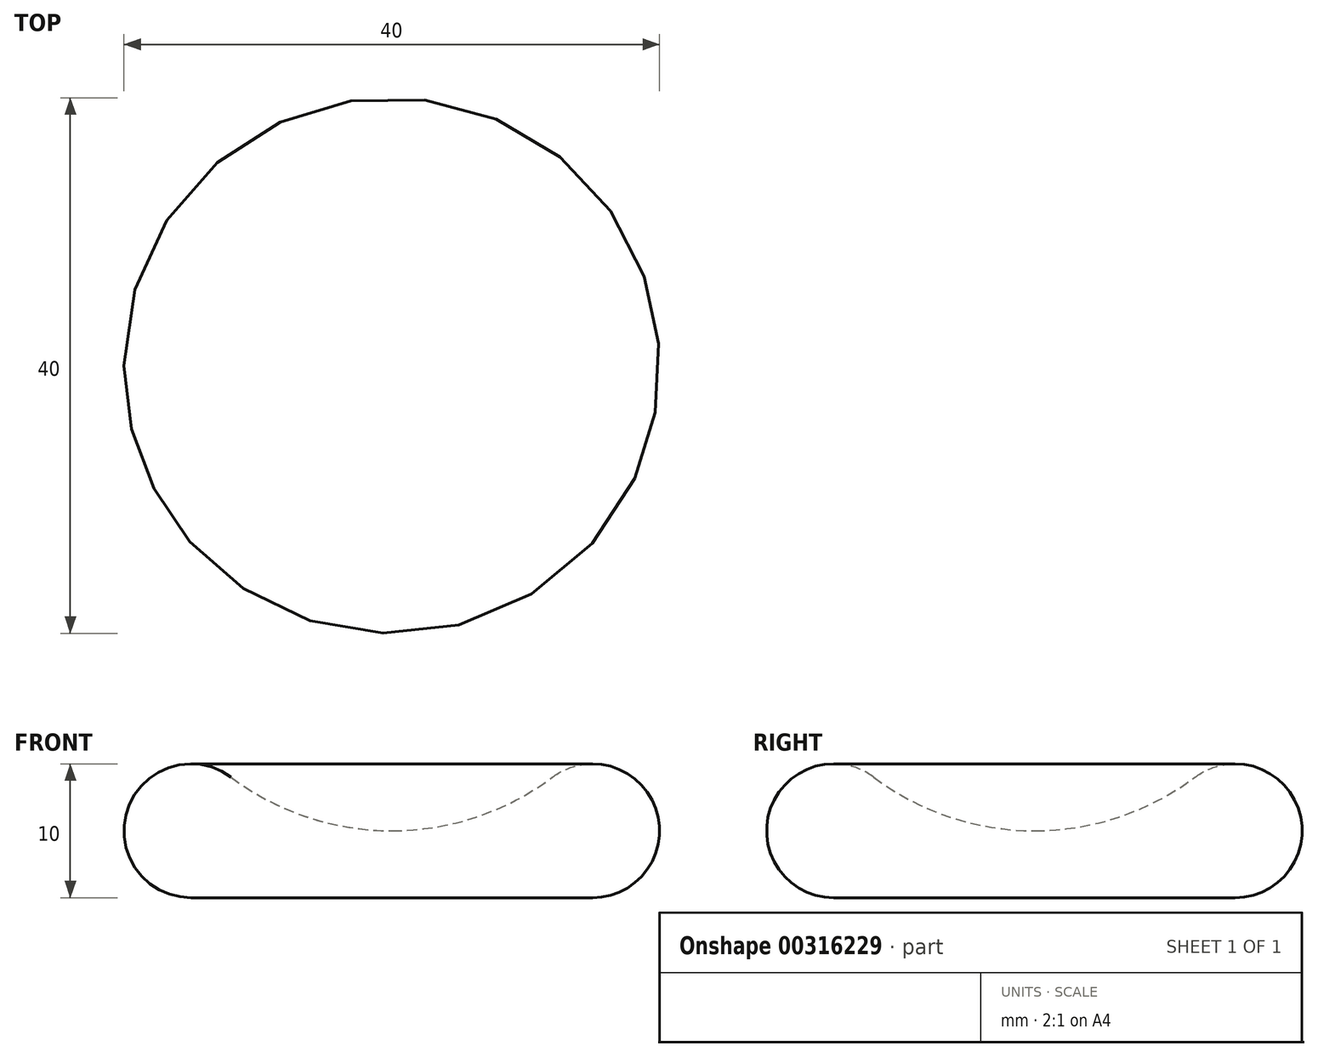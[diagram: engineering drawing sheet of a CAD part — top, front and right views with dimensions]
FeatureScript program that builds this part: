
annotation { "Feature Type Name" : "Feature", "Feature Type Description" : "" }
export const myFeature = defineFeature(function(context is Context, id is Id, definition is map)
    precondition{}
    {
        {
            var Q0;
            Q0=qCreatedBy(makeId("Front.planeOp"),FACE);
            var sketch = newSketch(context, id + "F0", { "sketchPlane" : qUnion([Q0])});
            skArc(sketch, "E0", {"start": v(-12, 9) * mm, "mid": v(-6.32, 6.03) * mm, "end": v(0, 5) * mm});
            skArc(sketch, "E1", {"start": v(-12, 9) * mm, "mid": v(-19.74, 6.58) * mm, "end": v(-15, 0) * mm});
            skLineSegment(sketch, "E2", {"start": v(0, 0) * mm, "end": v(0, 5) * mm});
            skLineSegment(sketch, "E3", {"start": v(0, 0) * mm, "end": v(-15, 0) * mm});
            skSolve(sketch);
        }
        {
            var Q0;
            Q0 = qSketchRegion(id + "F0", true);
            var Q1;
            Q1=sQuery(id+"F0.wireOp",EDGE,"E2");
            revolve(context, id + "F1", {"entities" : qUnion([Q0]), "axis" : qUnion([Q1]), "revolveType" : RevolveType.FULL});
        }
    });
